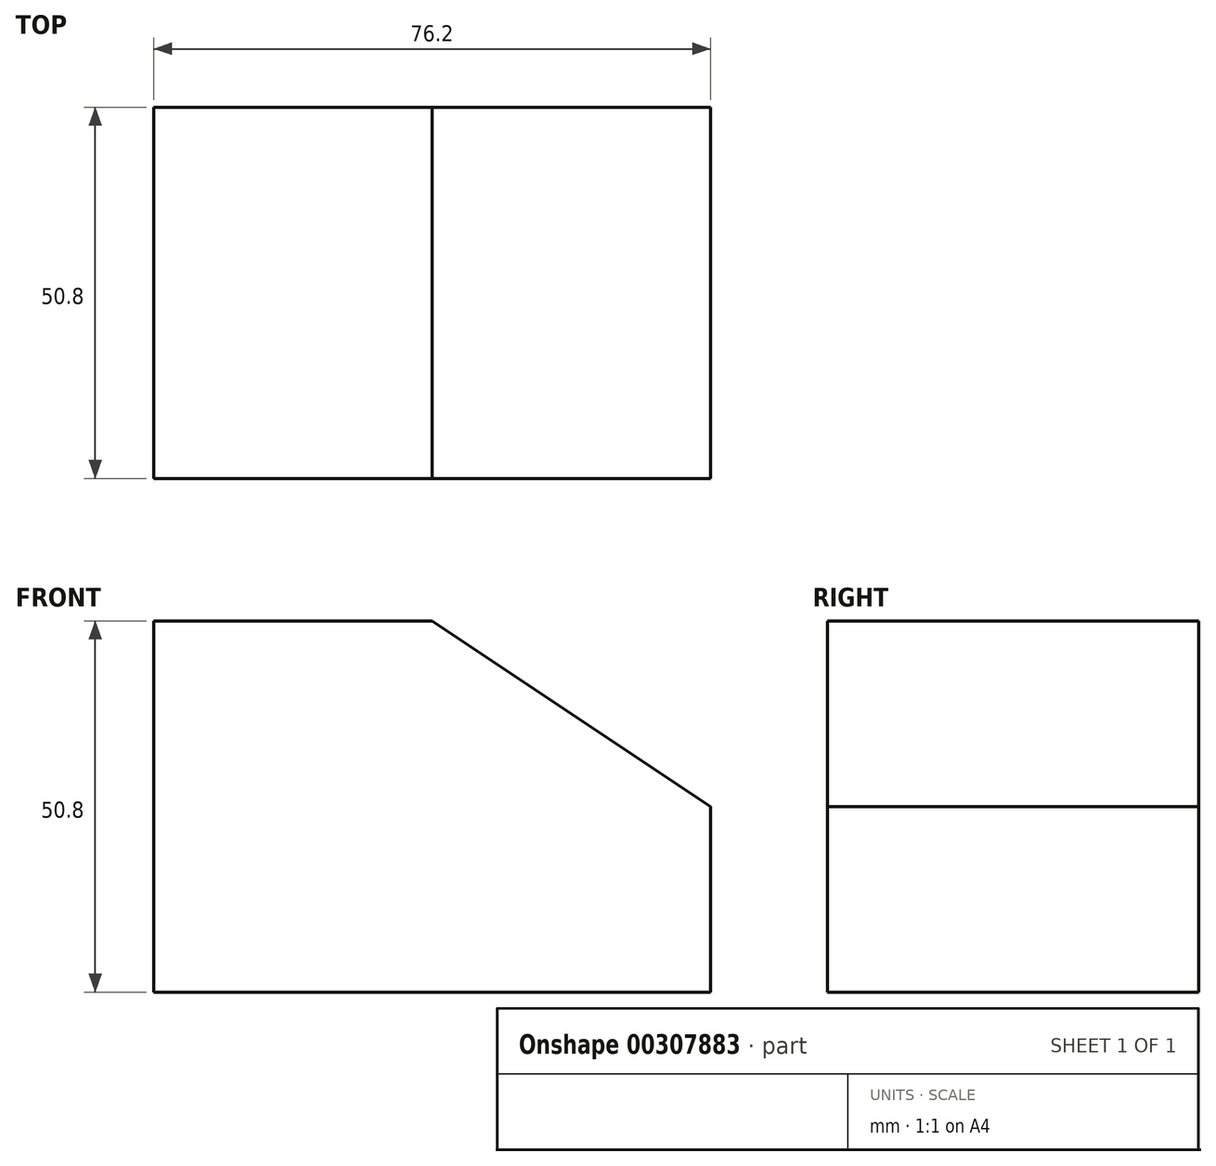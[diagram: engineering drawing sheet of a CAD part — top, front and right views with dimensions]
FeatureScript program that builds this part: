
annotation { "Feature Type Name" : "Feature", "Feature Type Description" : "" }
export const myFeature = defineFeature(function(context is Context, id is Id, definition is map)
    precondition{}
    {
        {
            var Q0;
            Q0=qCreatedBy(makeId("Front.planeOp"),FACE);
            var sketch = newSketch(context, id + "F0", { "sketchPlane" : qUnion([Q0])});
            skLineSegment(sketch, "E0", {"start": v(-34.85, -21.81) * mm, "end": v(41.35, -21.81) * mm});
            skLineSegment(sketch, "E1", {"start": v(41.35, -21.81) * mm, "end": v(41.35, 3.59) * mm});
            skLineSegment(sketch, "E2", {"start": v(-34.85, -21.81) * mm, "end": v(-34.85, 28.99) * mm});
            skLineSegment(sketch, "E3", {"start": v(-34.85, 28.99) * mm, "end": v(3.25, 28.99) * mm});
            skLineSegment(sketch, "E4", {"start": v(3.25, 28.99) * mm, "end": v(41.35, 3.59) * mm});
            skSolve(sketch);
        }
        {
            var Q0;
            Q0=makeQuery(id+"F0.imprint","IMPRINT",FACE,{"disambiguationData":[TD([[makeQuery(id+"F0.imprint","IMPRINT",EDGE,{"derivedFrom":sQuery(id+"F0.wireOp",EDGE,"E0")}),1.0]])]});
            extrude(context, id + "F1", {"entities" : qUnion([Q0]), "depth" : 50.8 * mm});
        }
    });
